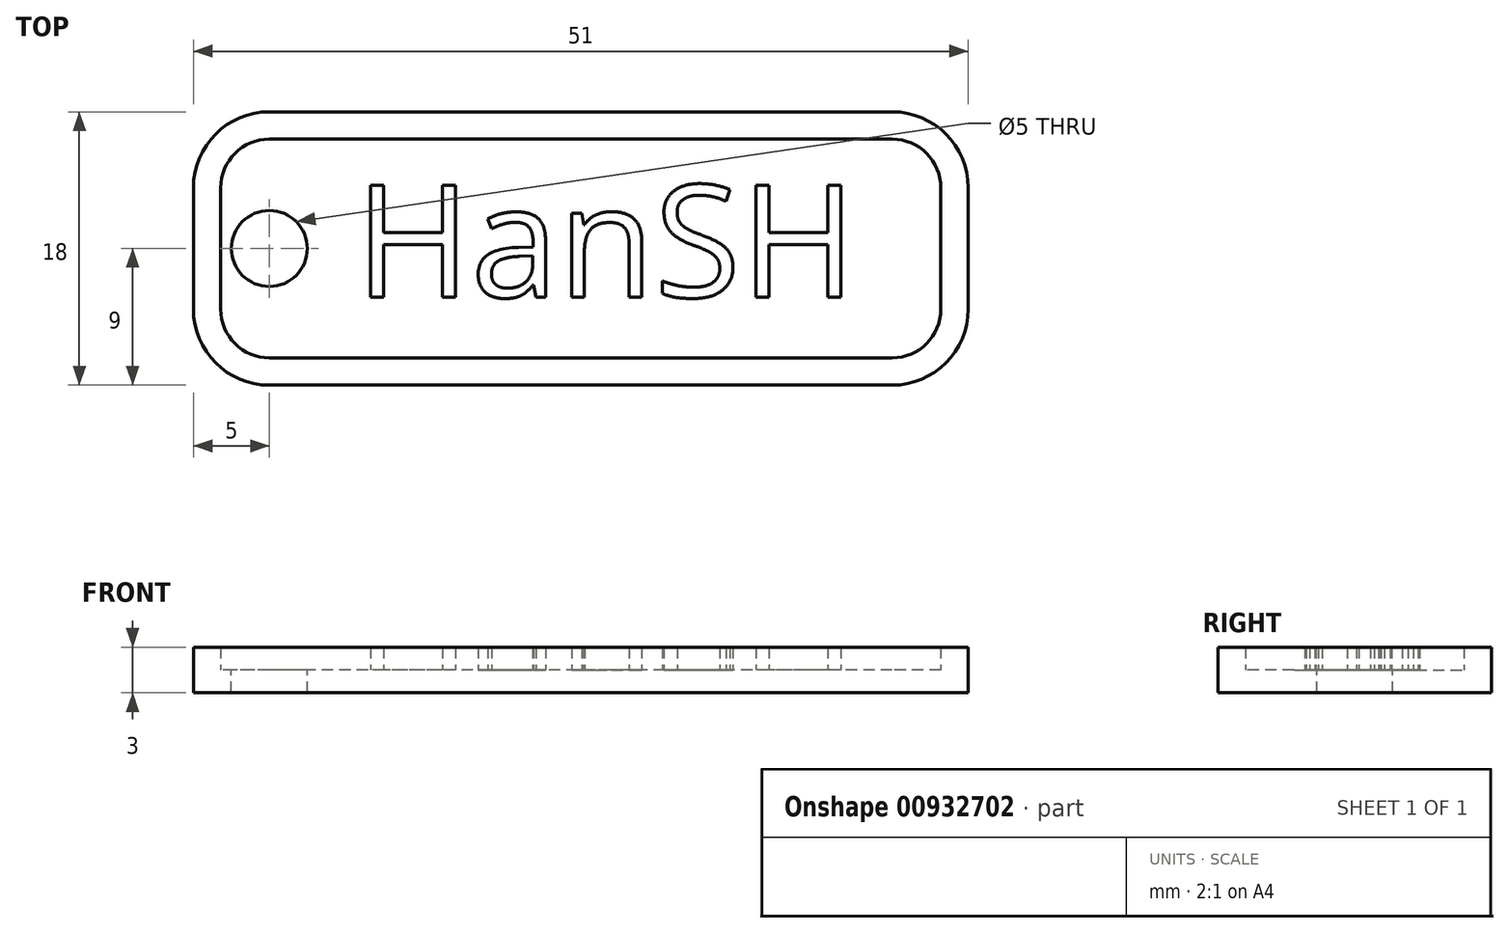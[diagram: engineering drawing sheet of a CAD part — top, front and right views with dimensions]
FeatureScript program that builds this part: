
annotation { "Feature Type Name" : "Feature", "Feature Type Description" : "" }
export const myFeature = defineFeature(function(context is Context, id is Id, definition is map)
    precondition{}
    {
        {
            var Q0;
            Q0=qCreatedBy(makeId("Top.planeOp"),FACE);
            var sketch = newSketch(context, id + "F0", { "sketchPlane" : qUnion([Q0])});
            skLineSegment(sketch, "E0.bottom", {"start": v(5, 0) * mm, "end": v(46, 0) * mm});
            skLineSegment(sketch, "E0.top", {"start": v(5, 18) * mm, "end": v(46, 18) * mm});
            skLineSegment(sketch, "E0.left", {"start": v(0, 5) * mm, "end": v(0, 13) * mm});
            skLineSegment(sketch, "E0.right", {"start": v(51, 5) * mm, "end": v(51, 13) * mm});
            skPoint(sketch, "E1.visualSharp", {"position": v(0, 18) * mm});
            skArc(sketch, "E1.filletArc", {"start": v(5, 18) * mm, "mid": v(1.46, 16.54) * mm, "end": v(0, 13) * mm});
            skPoint(sketch, "E2.visualSharp", {"position": v(51, 18) * mm});
            skArc(sketch, "E2.filletArc", {"start": v(51, 13) * mm, "mid": v(49.54, 16.54) * mm, "end": v(46, 18) * mm});
            skPoint(sketch, "E3.visualSharp", {"position": v(51, 0) * mm});
            skArc(sketch, "E3.filletArc", {"start": v(46, 0) * mm, "mid": v(49.54, 1.46) * mm, "end": v(51, 5) * mm});
            skPoint(sketch, "E4.visualSharp", {"position": v(0, 0) * mm});
            skArc(sketch, "E4.filletArc", {"start": v(0, 5) * mm, "mid": v(1.46, 1.46) * mm, "end": v(5, 0) * mm});
            skSolve(sketch);
        }
        {
            var Q0;
            Q0=makeQuery(id+"F0.imprint","IMPRINT",FACE,{"disambiguationData":[TD([[makeQuery(id+"F0.imprint","IMPRINT",EDGE,{"derivedFrom":sQuery(id+"F0.wireOp",EDGE,"E0.bottom")}),1.0]])]});
            extrude(context, id + "F1", {"entities" : qUnion([Q0]), "depth" : 1.5 * mm, "offsetDistance" : 25 * mm});
        }
        {
            var Q0;
            Q0=makeQuery(id+"F1.opExtrude","CAP_FACE",FACE,{"disambiguationData":[OSD([sQuery(id+"F0.wireOp",EDGE,"E0.bottom"),sQuery(id+"F0.wireOp",EDGE,"E0.top"),sQuery(id+"F0.wireOp",EDGE,"E0.left"),sQuery(id+"F0.wireOp",EDGE,"E0.right"),sQuery(id+"F0.wireOp",EDGE,"E1.filletArc"),sQuery(id+"F0.wireOp",EDGE,"E2.filletArc"),sQuery(id+"F0.wireOp",EDGE,"E3.filletArc"),sQuery(id+"F0.wireOp",EDGE,"E4.filletArc")])],"isStart":false});
            var sketch = newSketch(context, id + "F2", { "sketchPlane" : qUnion([Q0])});
            skArc(sketch, "E5.0", {"start": v(49.2, 13) * mm, "mid": v(48.26, 15.26) * mm, "end": v(46, 16.2) * mm});
            skLineSegment(sketch, "E5.1", {"start": v(49.2, 5) * mm, "end": v(49.2, 13) * mm});
            skLineSegment(sketch, "E5.2", {"start": v(46, 16.2) * mm, "end": v(5, 16.2) * mm});
            skArc(sketch, "E5.3", {"start": v(46, 1.8) * mm, "mid": v(48.26, 2.74) * mm, "end": v(49.2, 5) * mm});
            skArc(sketch, "E5.4", {"start": v(5, 16.2) * mm, "mid": v(2.74, 15.26) * mm, "end": v(1.8, 13) * mm});
            skLineSegment(sketch, "E5.5", {"start": v(1.8, 13) * mm, "end": v(1.8, 5) * mm});
            skArc(sketch, "E5.6", {"start": v(1.8, 5) * mm, "mid": v(2.74, 2.74) * mm, "end": v(5, 1.8) * mm});
            skLineSegment(sketch, "E5.7", {"start": v(5, 1.8) * mm, "end": v(46, 1.8) * mm});
            skSolve(sketch);
        }
        {
            var Q0;
            Q0=makeQuery(id+"F2.imprint","IMPRINT",FACE,{"disambiguationData":[TD([[makeQuery(id+"F2.imprint","IMPRINT",EDGE,{"derivedFrom":sQuery(id+"F2.wireOp",EDGE,"E5.0")}),-1.0]])]});
            extrude(context, id + "F3", {"entities" : qUnion([Q0]), "operationType" : NewBodyOperationType.ADD, "depth" : 1.5 * mm, "offsetDistance" : 25 * mm});
        }
        {
            var Q0;
            Q0=makeQuery(id+"F1.opExtrude","CAP_FACE",FACE,{"disambiguationData":[OSD([sQuery(id+"F0.wireOp",EDGE,"E0.bottom"),sQuery(id+"F0.wireOp",EDGE,"E0.top"),sQuery(id+"F0.wireOp",EDGE,"E0.left"),sQuery(id+"F0.wireOp",EDGE,"E0.right"),sQuery(id+"F0.wireOp",EDGE,"E1.filletArc"),sQuery(id+"F0.wireOp",EDGE,"E2.filletArc"),sQuery(id+"F0.wireOp",EDGE,"E3.filletArc"),sQuery(id+"F0.wireOp",EDGE,"E4.filletArc")])],"isStart":false});
            var sketch = newSketch(context, id + "F4", { "sketchPlane" : qUnion([Q0])});
            skCircle(sketch, "E6", {"center": v(5, 9) * mm, "radius": 2.5 * mm});
            skSolve(sketch);
        }
        {
            var Q0;
            Q0=makeQuery(id+"F4.imprint","IMPRINT",FACE,{"disambiguationData":[TD([[makeQuery(id+"F4.imprint","IMPRINT",EDGE,{"derivedFrom":sQuery(id+"F4.wireOp",EDGE,"E6")}),1.0]])]});
            extrude(context, id + "F5", {"entities" : qUnion([Q0]), "operationType" : NewBodyOperationType.REMOVE, "oppositeDirection" : true, "depth" : 25 * mm, "offsetDistance" : 25 * mm});
        }
        {
            var Q0;
            Q0=makeQuery(id+"F1.opExtrude","CAP_FACE",FACE,{"disambiguationData":[OSD([sQuery(id+"F0.wireOp",EDGE,"E0.bottom"),sQuery(id+"F0.wireOp",EDGE,"E0.top"),sQuery(id+"F0.wireOp",EDGE,"E0.left"),sQuery(id+"F0.wireOp",EDGE,"E0.right"),sQuery(id+"F0.wireOp",EDGE,"E1.filletArc"),sQuery(id+"F0.wireOp",EDGE,"E2.filletArc"),sQuery(id+"F0.wireOp",EDGE,"E3.filletArc"),sQuery(id+"F0.wireOp",EDGE,"E4.filletArc")])],"isStart":false});
            var sketch = newSketch(context, id + "F6", { "sketchPlane" : qUnion([Q0])});
            skText(sketch, "E7", { "text": "HanSH", "fontName": "OpenSans-Regular.ttf"});
            const initialGuessF6  = {"E7": [0.01066, 0.0058, 1, 0, 0.00743]};
            skSetInitialGuess(sketch, initialGuessF6);
            skSolve(sketch);
        }
        {
            var Q0;
            Q0 = qSketchRegion(id + "F6", true);
            extrude(context, id + "F7", {"entities" : qUnion([Q0]), "operationType" : NewBodyOperationType.ADD, "depth" : 1.5 * mm, "offsetDistance" : 25 * mm});
        }
    });
